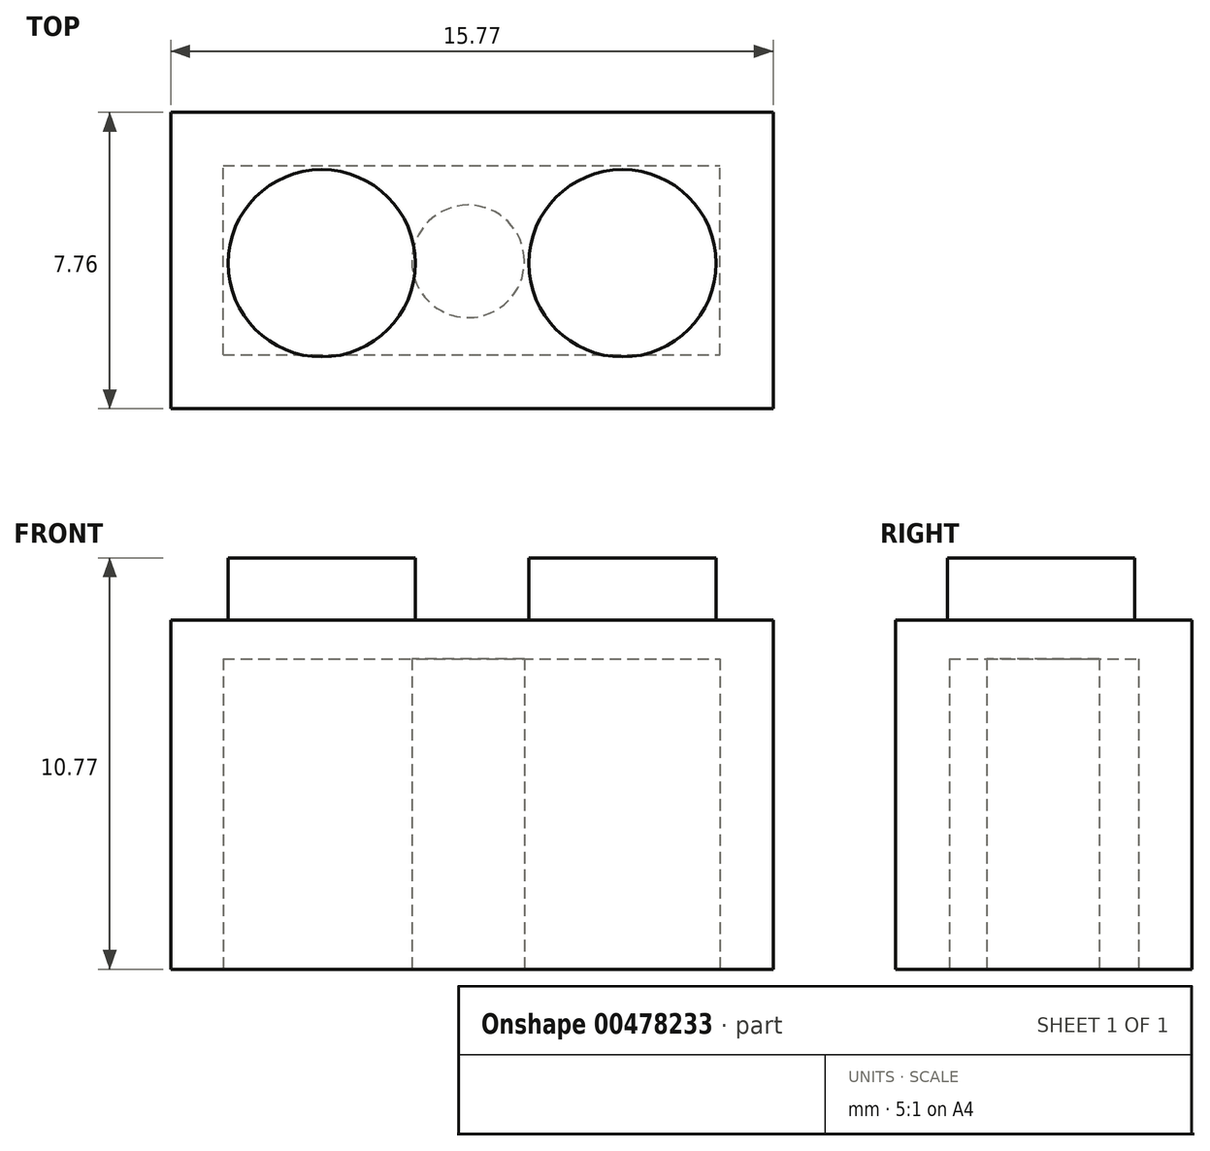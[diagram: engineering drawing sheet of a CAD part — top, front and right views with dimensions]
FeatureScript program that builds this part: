
annotation { "Feature Type Name" : "Feature", "Feature Type Description" : "" }
export const myFeature = defineFeature(function(context is Context, id is Id, definition is map)
    precondition{}
    {
        {
            var Q0;
            Q0=qCreatedBy(makeId("Top.planeOp"),FACE);
            var sketch = newSketch(context, id + "F0", { "sketchPlane" : qUnion([Q0])});
            skLineSegment(sketch, "E0.bottom", {"start": v(-8.24, -18.24) * mm, "end": v(7.53, -18.24) * mm});
            skLineSegment(sketch, "E0.top", {"start": v(-8.24, -26) * mm, "end": v(7.53, -26) * mm});
            skLineSegment(sketch, "E0.left", {"start": v(-8.24, -18.24) * mm, "end": v(-8.24, -26) * mm});
            skLineSegment(sketch, "E0.right", {"start": v(7.53, -18.24) * mm, "end": v(7.53, -26) * mm});
            skSolve(sketch);
        }
        {
            var Q0;
            Q0=makeQuery(id+"F0.imprint","IMPRINT",FACE,{"disambiguationData":[TD([[makeQuery(id+"F0.imprint","IMPRINT",EDGE,{"derivedFrom":sQuery(id+"F0.wireOp",EDGE,"E0.bottom")}),-1.0]])]});
            var Q1;
            Q1 = qSketchRegion(id + "F2", true);
            extrude(context, id + "F1", {"entities" : qUnion([Q0, Q1]), "depth" : 9.14 * mm});
        }
        {
            var Q0;
            Q0=makeQuery(id+"F1.opExtrude","CAP_FACE",FACE,{"disambiguationData":[OSD([sQuery(id+"F0.wireOp",EDGE,"E0.bottom"),sQuery(id+"F0.wireOp",EDGE,"E0.top"),sQuery(id+"F0.wireOp",EDGE,"E0.left"),sQuery(id+"F0.wireOp",EDGE,"E0.right")])],"isStart":false});
            var sketch = newSketch(context, id + "F2", { "sketchPlane" : qUnion([Q0])});
            skCircle(sketch, "E1", {"center": v(-4.3, -22.19) * mm, "radius": 2.45 * mm});
            skCircle(sketch, "E2", {"center": v(3.58, -22.19) * mm, "radius": 2.45 * mm});
            skSolve(sketch);
        }
        {
            var Q0;
            Q0 = qSketchRegion(id + "F2", true);
            extrude(context, id + "F3", {"entities" : qUnion([Q0]), "operationType" : NewBodyOperationType.ADD, "depth" : 1.63 * mm});
        }
        {
            var Q0;
            Q0=makeQuery(id+"F1.opExtrude","CAP_FACE",FACE,{"disambiguationData":[OSD([sQuery(id+"F0.wireOp",EDGE,"E0.bottom"),sQuery(id+"F0.wireOp",EDGE,"E0.top"),sQuery(id+"F0.wireOp",EDGE,"E0.left"),sQuery(id+"F0.wireOp",EDGE,"E0.right")])],"isStart":true});
            var sketch = newSketch(context, id + "F4", { "sketchPlane" : qUnion([Q0])});
            skCircle(sketch, "E3", {"center": v(-1.56, 22.56) * mm, "radius": 0.01 * mm});
            skSolve(sketch);
        }
        {
            var Q0;
            Q0=makeQuery(id+"F4.imprint","IMPRINT",FACE,{"disambiguationData":[TD([[makeQuery(id+"F4.imprint","IMPRINT",EDGE,{"derivedFrom":sQuery(id+"F4.wireOp",EDGE,"E3")}),-1.0]])]});
            var sketch = newSketch(context, id + "F5", { "sketchPlane" : qUnion([Q0])});
            skLineSegment(sketch, "E4.bottom", {"start": v(-6.87, 24.6) * mm, "end": v(6.14, 24.6) * mm});
            skLineSegment(sketch, "E4.top", {"start": v(-6.87, 19.64) * mm, "end": v(6.14, 19.64) * mm});
            skLineSegment(sketch, "E4.left", {"start": v(-6.87, 24.6) * mm, "end": v(-6.87, 19.64) * mm});
            skLineSegment(sketch, "E4.right", {"start": v(6.14, 24.6) * mm, "end": v(6.14, 19.64) * mm});
            skSolve(sketch);
        }
        {
            var Q0;
            Q0 = qSketchRegion(id + "F5", true);
            extrude(context, id + "F6", {"entities" : qUnion([Q0]), "operationType" : NewBodyOperationType.REMOVE, "oppositeDirection" : true, "depth" : 8.13 * mm});
        }
        {
            var Q0;
            Q0=makeQuery(id+"F4.imprint","IMPRINT",FACE,{"disambiguationData":[TD([[makeQuery(id+"F4.imprint","IMPRINT",EDGE,{"derivedFrom":sQuery(id+"F4.wireOp",EDGE,"E3")}),1.0]])]});
            var sketch = newSketch(context, id + "F7", { "sketchPlane" : qUnion([Q0])});
            skCircle(sketch, "E5", {"center": v(-0.26, 22.15) * mm, "radius": 1.55 * mm});
            skSolve(sketch);
        }
        {
            var Q0;
            Q0 = qSketchRegion(id + "F7", true);
            extrude(context, id + "F8", {"entities" : qUnion([Q0]), "depth" : -8.13 * mm, "offsetDistance" : 25.4 * mm});
        }
        {
            var Q0;
            Q0=makeQuery(id+"F8.opExtrude","SWEPT_BODY",BODY,{"disambiguationData":[OSD([sQuery(id+"F7.wireOp",EDGE,"E5")])]});
            deleteBodies(context, id + "F9", {"entities" : qUnion([Q0])});
        }
        {
            var Q0;
            Q0=qCreatedBy(makeId("Top.planeOp"),FACE);
            var sketch = newSketch(context, id + "F10", { "sketchPlane" : qUnion([Q0])});
            skCircle(sketch, "E6", {"center": v(-0.46, -22.14) * mm, "radius": 1.47 * mm});
            skSolve(sketch);
        }
        {
            var Q0;
            Q0 = qSketchRegion(id + "F10", true);
            extrude(context, id + "F11", {"entities" : qUnion([Q0]), "operationType" : NewBodyOperationType.ADD, "depth" : 8.13 * mm, "offsetDistance" : 25.4 * mm});
        }
    });
